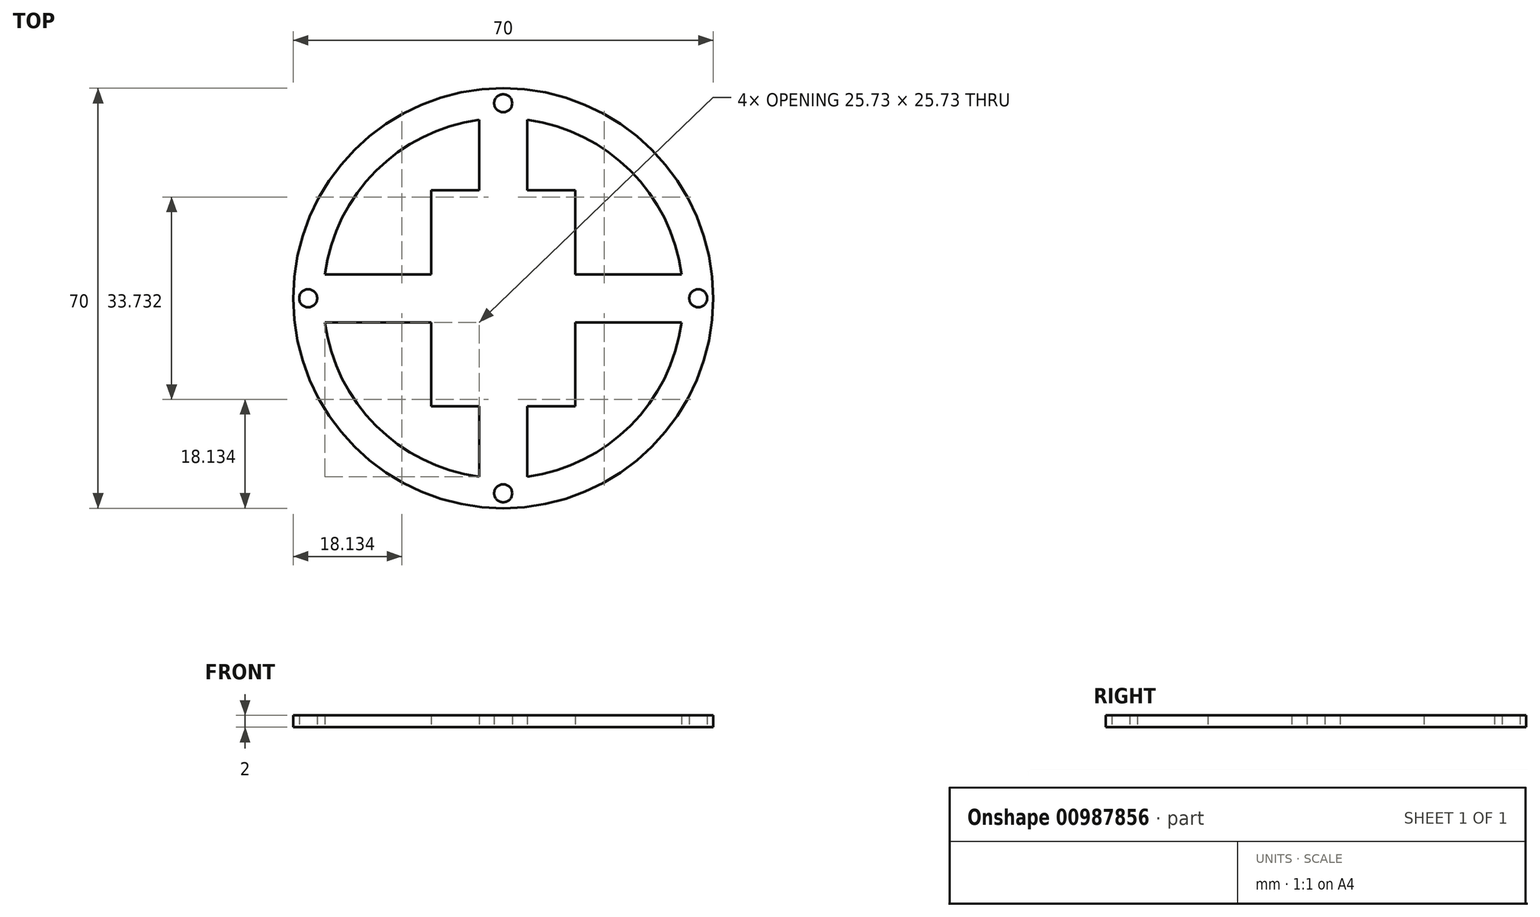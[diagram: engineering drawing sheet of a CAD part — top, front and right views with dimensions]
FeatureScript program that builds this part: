
annotation { "Feature Type Name" : "Feature", "Feature Type Description" : "" }
export const myFeature = defineFeature(function(context is Context, id is Id, definition is map)
    precondition{}
    {
        {
            var Q0;
            Q0=qCreatedBy(makeId("Top.planeOp"),FACE);
            var sketch = newSketch(context, id + "F0", { "sketchPlane" : qUnion([Q0])});
            skCircle(sketch, "E0", {"center": v(0, 0) * mm, "radius": 35 * mm});
            skCircle(sketch, "E1", {"center": v(0, 0) * mm, "radius": 30 * mm});
            skLineSegment(sketch, "E2", {"start": v(-9.84, 16.24) * mm, "end": v(-9.84, -15.76) * mm});
            skLineSegment(sketch, "E3", {"start": v(-9.84, -15.76) * mm, "end": v(10.14, -15.76) * mm});
            skLineSegment(sketch, "E4", {"start": v(10.14, -15.76) * mm, "end": v(10.14, 16.24) * mm});
            skLineSegment(sketch, "E5", {"start": v(10.14, 16.24) * mm, "end": v(-9.86, 16.24) * mm});
            skLineSegment(sketch, "E6", {"start": v(-12, 18) * mm, "end": v(-12, -18) * mm});
            skLineSegment(sketch, "E7", {"start": v(-12, 18) * mm, "end": v(12, 18) * mm});
            skLineSegment(sketch, "E8", {"start": v(12, 18) * mm, "end": v(12, -18) * mm});
            skLineSegment(sketch, "E9", {"start": v(12, -18) * mm, "end": v(-12, -18) * mm});
            skLineSegment(sketch, "E10", {"start": v(-12, 4) * mm, "end": v(-12, 18) * mm});
            skLineSegment(sketch, "E11", {"start": v(12, 12.1) * mm, "end": v(12, -18) * mm});
            skLineSegment(sketch, "E12", {"start": v(4, -18) * mm, "end": v(12, -18) * mm});
            skLineSegment(sketch, "E13", {"start": v(-4, 29.73) * mm, "end": v(-4, 18) * mm});
            skLineSegment(sketch, "E14", {"start": v(-4, 18) * mm, "end": v(-12, 18) * mm});
            skLineSegment(sketch, "E15", {"start": v(-12, -18) * mm, "end": v(-4, -18) * mm});
            skLineSegment(sketch, "E16", {"start": v(-4, -18) * mm, "end": v(-4, -29.73) * mm});
            skLineSegment(sketch, "E17", {"start": v(4, -29.73) * mm, "end": v(4, -18) * mm});
            skLineSegment(sketch, "E18", {"start": v(12, -18) * mm, "end": v(12, 18) * mm});
            skLineSegment(sketch, "E19", {"start": v(4, 18) * mm, "end": v(4, 29.73) * mm});
            skLineSegment(sketch, "E20", {"start": v(-29.73, 4) * mm, "end": v(-12, 4) * mm});
            skLineSegment(sketch, "E21", {"start": v(12, -5.15) * mm, "end": v(12, -18) * mm});
            skLineSegment(sketch, "E22", {"start": v(-12, -18) * mm, "end": v(-12, -4) * mm});
            skLineSegment(sketch, "E23", {"start": v(-12, -4) * mm, "end": v(-29.73, -4) * mm});
            skCircle(sketch, "E24", {"center": v(0, 32.5) * mm, "radius": 1.5 * mm});
            skCircle(sketch, "E25", {"center": v(-32.5, 0) * mm, "radius": 1.5 * mm});
            skCircle(sketch, "E26", {"center": v(32.5, 0) * mm, "radius": 1.5 * mm});
            skCircle(sketch, "E27", {"center": v(0, -32.5) * mm, "radius": 1.5 * mm});
            skLineSegment(sketch, "E28", {"start": v(-28.44, 4) * mm, "end": v(-28.44, 0) * mm, "construction": true});
            skLineSegment(sketch, "E29", {"start": v(-28.44, 0) * mm, "end": v(-28.44, -4) * mm, "construction": true});
            skLineSegment(sketch, "E30.MirrorCS", {"start": v(29.73, 4) * mm, "end": v(12, 4) * mm});
            skLineSegment(sketch, "E31.MirrorCS", {"start": v(12, -4) * mm, "end": v(29.73, -4) * mm});
            skLineSegment(sketch, "E32", {"start": v(-4, 33.6) * mm, "end": v(0, 33.6) * mm, "construction": true});
            skLineSegment(sketch, "E33", {"start": v(0, 33.6) * mm, "end": v(4, 33.6) * mm, "construction": true});
            skLineSegment(sketch, "E34", {"start": v(-32.5, 0) * mm, "end": v(0, 0) * mm, "construction": true});
            skLineSegment(sketch, "E35", {"start": v(0, 0) * mm, "end": v(32.5, 0) * mm, "construction": true});
            skLineSegment(sketch, "E36", {"start": v(0, 0) * mm, "end": v(0, -32.5) * mm, "construction": true});
            skLineSegment(sketch, "E37", {"start": v(0, 32.5) * mm, "end": v(0, 0) * mm, "construction": true});
            skSolve(sketch);
        }
        {
            var Q0;
            Q0=makeQuery(id+"F0.imprint","IMPRINT",FACE,{"disambiguationData":[TD([[makeQuery(id+"F0.imprint","IMPRINT",EDGE,{"derivedFrom":sQuery(id+"F0.wireOp",EDGE,"E0")}),1.0]])]});
            var Q1;
            {var subQ0=sQuery(id+"F0.wireOp",EDGE,"E13");Q1=makeQuery(id+"F0.imprint","IMPRINT",FACE,{"disambiguationData":[TD([[makeQuery(id+"F0.imprint","IMPRINT",EDGE,{"derivedFrom":subQ0}),1.0]])]});}
            var Q2;
            Q2=makeQuery(id+"F0.imprint","IMPRINT",FACE,{"disambiguationData":[TD([[makeQuery(id+"F0.imprint","IMPRINT",EDGE,{"derivedFrom":sQuery(id+"F0.wireOp",EDGE,"E6")}),-1.0]])]});
            var Q3;
            {var subQ0=sQuery(id+"F0.wireOp",EDGE,"ZGUPFVcQ-Tey6-lDge-y4ng-aYvP5VUUE1ul");Q3=makeQuery(id+"F0.imprint","IMPRINT",FACE,{"disambiguationData":[TD([[makeQuery(id+"F0.imprint","IMPRINT",EDGE,{"derivedFrom":subQ0}),-1.0]])]});}
            var Q4;
            Q4=makeQuery(id+"F0.imprint","IMPRINT",FACE,{"disambiguationData":[TD([[makeQuery(id+"F0.imprint","IMPRINT",EDGE,{"derivedFrom":sQuery(id+"F0.wireOp",EDGE,"E9")}),1.0]])]});
            var Q5;
            {var subQ3=sQuery(id+"F0.wireOp",EDGE,"E2");Q5=makeQuery(id+"F0.imprint","IMPRINT",FACE,{"disambiguationData":[TD([[makeQuery(id+"F0.imprint","IMPRINT",EDGE,{"derivedFrom":subQ3}),-1.0]])]});}
            var Q6;
            {var subQ0=sQuery(id+"F0.wireOp",EDGE,"E2");Q6=makeQuery(id+"F0.imprint","IMPRINT",FACE,{"disambiguationData":[TD([[makeQuery(id+"F0.imprint","IMPRINT",EDGE,{"derivedFrom":subQ0}),1.0]])]});}
            var Q7;
            {var subQ2=sQuery(id+"F0.wireOp",EDGE,"OV2fNkNx-53DJ-fSKS-1mRz-XQc7H1Hk84CO");Q7=makeQuery(id+"F0.imprint","IMPRINT",FACE,{"disambiguationData":[TD([[makeQuery(id+"F0.imprint","IMPRINT",EDGE,{"derivedFrom":subQ2}),-1.0]])]});}
            var Q8;
            {var subQ0=sQuery(id+"F0.wireOp",EDGE,"E30.MirrorCS");Q8=makeQuery(id+"F0.imprint","IMPRINT",FACE,{"disambiguationData":[TD([[makeQuery(id+"F0.imprint","IMPRINT",EDGE,{"derivedFrom":subQ0}),1.0]])]});}
            extrude(context, id + "F1", {"entities" : qUnion([Q0, Q1, Q2, Q3, Q4, Q5, Q6, Q7, Q8]), "depth" : 2 * mm, "offsetDistance" : 25 * mm});
        }
    });
